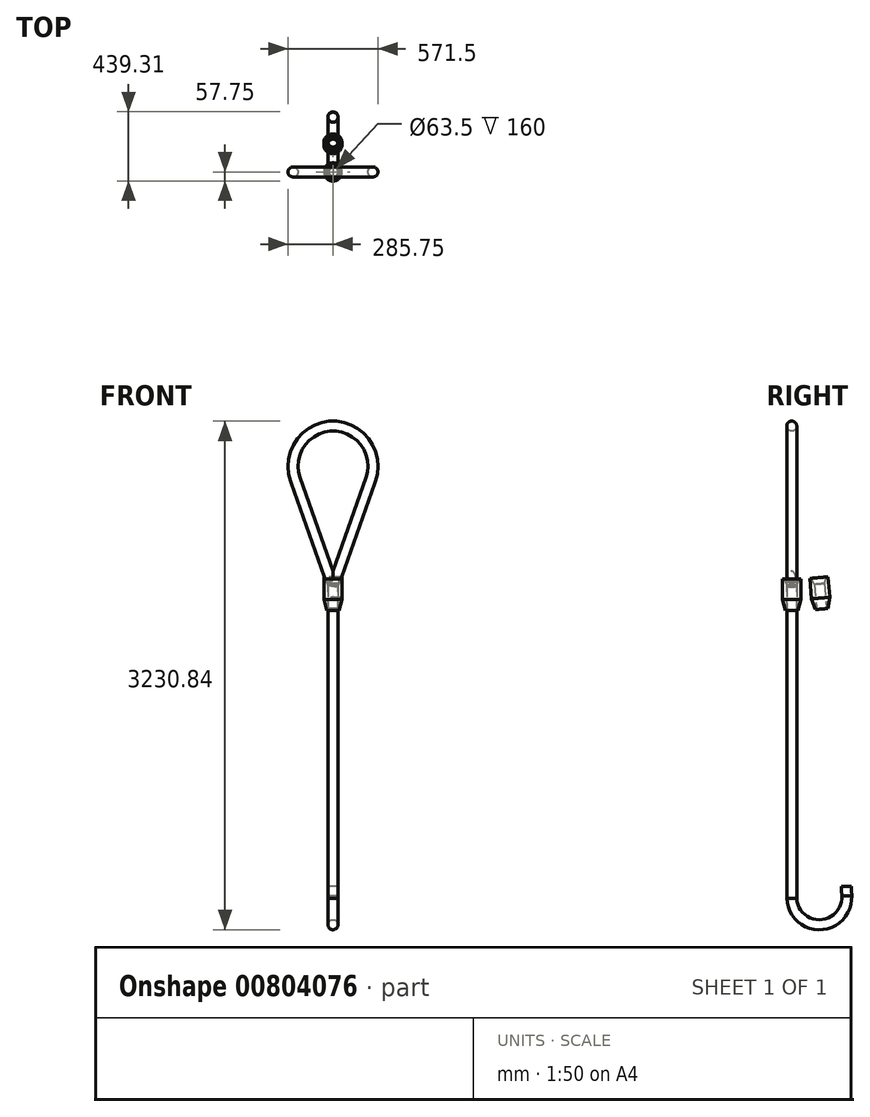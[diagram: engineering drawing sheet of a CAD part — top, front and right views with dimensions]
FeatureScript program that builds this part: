
annotation { "Feature Type Name" : "Feature", "Feature Type Description" : "" }
export const myFeature = defineFeature(function(context is Context, id is Id, definition is map)
    precondition{}
    {
        {
            var Q0;
            Q0=qCreatedBy(makeId("Top.planeOp"),FACE);
            var sketch = newSketch(context, id + "F0", { "sketchPlane" : qUnion([Q0])});
            skCircle(sketch, "E0", {"center": v(0, 0) * mm, "radius": 31.75 * mm});
            skSolve(sketch);
        }
        {
            var Q0;
            Q0=qCreatedBy(makeId("Front.planeOp"),FACE);
            var sketch = newSketch(context, id + "F1", { "sketchPlane" : qUnion([Q0])});
            skLineSegment(sketch, "E1", {"start": v(0, 0) * mm, "end": v(0, 1984) * mm});
            skLineSegment(sketch, "E2", {"start": v(0, 1984) * mm, "end": v(0, 3000) * mm, "construction": true});
            skLineSegment(sketch, "E3", {"start": v(0, 1984) * mm, "end": v(239.47, 2661.33) * mm});
            skArc(sketch, "E4", {"start": v(239.47, 2661.33) * mm, "mid": v(207.4, 2892.65) * mm, "end": v(0, 3000) * mm});
            skArc(sketch, "E5.MirrorCS", {"start": v(-239.47, 2661.33) * mm, "mid": v(-207.4, 2892.65) * mm, "end": v(0, 3000) * mm});
            skLineSegment(sketch, "E6", {"start": v(-239.47, 2661.33) * mm, "end": v(-11.6, 2016.8) * mm});
            skSolve(sketch);
        }
        {
            var Q0;
            Q0=makeQuery(id+"F0.imprint","IMPRINT",FACE,{"disambiguationData":[TD([[makeQuery(id+"F0.imprint","IMPRINT",EDGE,{"derivedFrom":sQuery(id+"F0.wireOp",EDGE,"E0")}),1.0]])]});
            var Q1;
            Q1=sQuery(id+"F1.wireOp",EDGE,"E1");
            var Q2;
            Q2=sQuery(id+"F1.wireOp",EDGE,"E3");
            var Q3;
            Q3=sQuery(id+"F1.wireOp",EDGE,"E4");
            var Q4;
            Q4=sQuery(id+"F1.wireOp",EDGE,"E5.MirrorCS");
            var Q5;
            Q5=sQuery(id+"F1.wireOp",EDGE,"E6");
            sweep(context, id + "F2", {"profiles" : qUnion([Q0]), "path" : qUnion([Q1, Q2, Q3, Q4, Q5])});
        }
        {
            var Q0;
            Q0=qCreatedBy(makeId("Front.planeOp"),FACE);
            var sketch = newSketch(context, id + "F3", { "sketchPlane" : qUnion([Q0])});
            skLineSegment(sketch, "E7", {"start": v(31.75, 1830) * mm, "end": v(31.75, 1990) * mm});
            skLineSegment(sketch, "E8", {"start": v(31.75, 1990) * mm, "end": v(47.75, 2030) * mm});
            skLineSegment(sketch, "E9", {"start": v(47.75, 2030) * mm, "end": v(57.75, 2030) * mm});
            skLineSegment(sketch, "E10", {"start": v(57.75, 2030) * mm, "end": v(57.75, 1900) * mm});
            skLineSegment(sketch, "E11", {"start": v(57.75, 1900) * mm, "end": v(39.75, 1830) * mm});
            skLineSegment(sketch, "E12", {"start": v(39.75, 1830) * mm, "end": v(31.75, 1830) * mm});
            skSolve(sketch);
        }
        {
            var Q0;
            Q0=qCreatedBy(makeId("Front.planeOp"),FACE);
            var sketch = newSketch(context, id + "F4", { "sketchPlane" : qUnion([Q0])});
            skLineSegment(sketch, "E13", {"start": v(0, 0) * mm, "end": v(0, 542.03) * mm});
            skSolve(sketch);
        }
        {
            var Q0;
            Q0=makeQuery(id+"F3.imprint","IMPRINT",FACE,{"disambiguationData":[TD([[makeQuery(id+"F3.imprint","IMPRINT",EDGE,{"derivedFrom":sQuery(id+"F3.wireOp",EDGE,"E7")}),-1.0]])]});
            var Q1;
            Q1=sQuery(id+"F4.wireOp",EDGE,"E13");
            revolve(context, id + "F5", {"surfaceOperationType" : NewSurfaceOperationType.NEW, "entities" : qUnion([Q0]), "axis" : qUnion([Q1]), "revolveType" : RevolveType.FULL});
        }
        {
            var Q0;
            Q0=qCreatedBy(makeId("Right.planeOp"),FACE);
            var sketch = newSketch(context, id + "F6", { "sketchPlane" : qUnion([Q0])});
            skLineSegment(sketch, "E14", {"start": v(0, 0) * mm, "end": v(300, 0) * mm, "construction": true});
            skLineSegment(sketch, "E15", {"start": v(0, 0) * mm, "end": v(349.67, 15.27) * mm, "construction": true});
            skCircle(sketch, "E16", {"center": v(174.83, 7.63) * mm, "radius": 175 * mm, "construction": true});
            skArc(sketch, "E17", {"start": v(0, 0) * mm, "mid": v(182.47, -167.2) * mm, "end": v(349.67, 15.27) * mm});
            skLineSegment(sketch, "E18", {"start": v(349.67, 15.27) * mm, "end": v(347.05, 75.2) * mm});
            skSolve(sketch);
        }
        {
            var Q0;
            Q0=sQuery(id+"F6.wireOp",EDGE,"E15");
            cPlane(context, id + "F7", {"entities" : qUnion([Q0]), "cplaneType" : CPlaneType.MID_PLANE, "offset" : 25 * mm, "width" : 150 * mm, "height" : 150 * mm});
        }
        {
            var Q0;
            Q0 = qSketchRegion(id + "F0", true);
            var Q1;
            Q1=sQuery(id+"F6.wireOp",EDGE,"E17");
            var Q2;
            Q2=sQuery(id+"F6.wireOp",EDGE,"E18");
            sweep(context, id + "F8", {"operationType" : NewBodyOperationType.ADD, "profiles" : qUnion([Q0]), "path" : qUnion([Q1, Q2])});
        }
        {
            var Q0;
            Q0=makeQuery(id+"F5.opRevolve","SWEPT_BODY",BODY,{"disambiguationData":[OSD([sQuery(id+"F3.wireOp",EDGE,"E7"),sQuery(id+"F3.wireOp",EDGE,"E8"),sQuery(id+"F3.wireOp",EDGE,"E9"),sQuery(id+"F3.wireOp",EDGE,"E10"),sQuery(id+"F3.wireOp",EDGE,"E11"),sQuery(id+"F3.wireOp",EDGE,"E12")])]});
            var Q1;
            Q1=qCreatedBy(id+"F7.planeOp",FACE);
            mirror(context, id + "F9", {"entities" : qUnion([Q0]), "mirrorPlane" : qUnion([Q1])});
        }
    });
